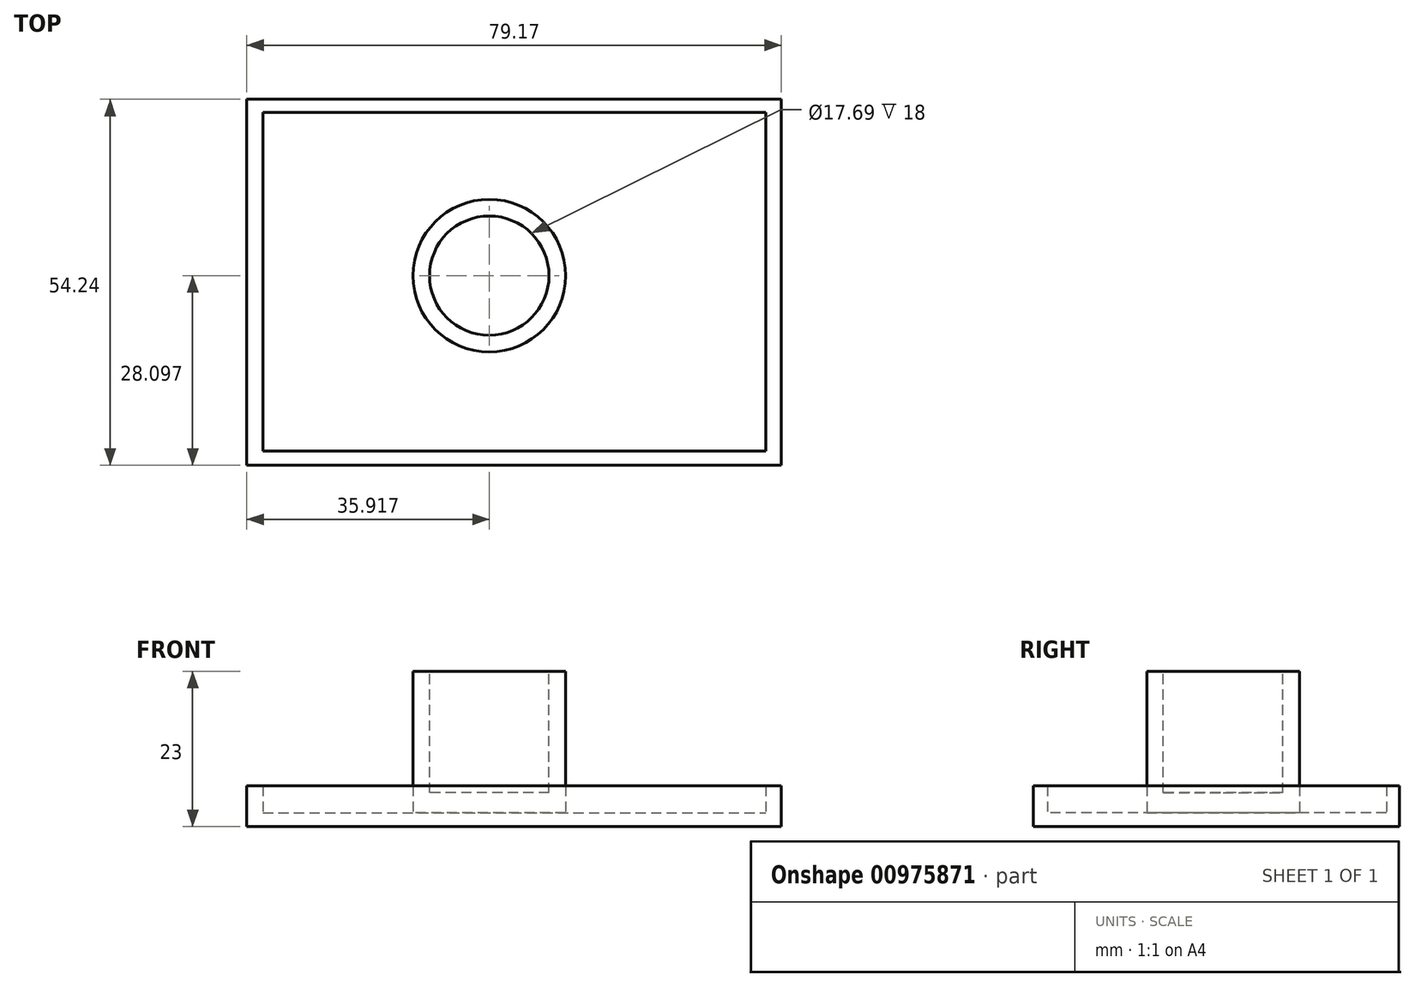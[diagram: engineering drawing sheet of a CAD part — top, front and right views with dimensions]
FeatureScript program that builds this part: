
annotation { "Feature Type Name" : "Feature", "Feature Type Description" : "" }
export const myFeature = defineFeature(function(context is Context, id is Id, definition is map)
    precondition{}
    {
        {
            var Q0;
            Q0=qCreatedBy(makeId("Top.planeOp"),FACE);
            var sketch = newSketch(context, id + "F0", { "sketchPlane" : qUnion([Q0])});
            skLineSegment(sketch, "E0.bottom", {"start": v(-67.35, 63.95) * mm, "end": v(11.82, 63.95) * mm});
            skLineSegment(sketch, "E0.top", {"start": v(-67.35, 9.7) * mm, "end": v(11.82, 9.7) * mm});
            skLineSegment(sketch, "E0.left", {"start": v(-67.35, 63.95) * mm, "end": v(-67.35, 9.7) * mm});
            skLineSegment(sketch, "E0.right", {"start": v(11.82, 63.95) * mm, "end": v(11.82, 9.7) * mm});
            skSolve(sketch);
        }
        {
            var Q0;
            Q0=makeQuery(id+"F0.imprint","IMPRINT",FACE,{"disambiguationData":[TD([[makeQuery(id+"F0.imprint","IMPRINT",EDGE,{"derivedFrom":sQuery(id+"F0.wireOp",EDGE,"E0.bottom")}),-1.0]])]});
            extrude(context, id + "F1", {"entities" : qUnion([Q0]), "depth" : 2 * mm, "offsetDistance" : 25 * mm});
        }
        {
            var Q0;
            Q0=makeQuery(id+"F1.opExtrude","CAP_FACE",FACE,{"disambiguationData":[OSD([sQuery(id+"F0.wireOp",EDGE,"E0.bottom"),sQuery(id+"F0.wireOp",EDGE,"E0.top"),sQuery(id+"F0.wireOp",EDGE,"E0.left"),sQuery(id+"F0.wireOp",EDGE,"E0.right")])],"isStart":false});
            var sketch = newSketch(context, id + "F2", { "sketchPlane" : qUnion([Q0])});
            skLineSegment(sketch, "E1.bottom", {"start": v(-67.35, 63.95) * mm, "end": v(11.82, 63.95) * mm});
            skLineSegment(sketch, "E1.top", {"start": v(-67.35, 62.02) * mm, "end": v(11.82, 62.02) * mm});
            skLineSegment(sketch, "E1.left", {"start": v(-67.35, 63.95) * mm, "end": v(-67.35, 62.02) * mm});
            skLineSegment(sketch, "E1.right", {"start": v(11.82, 63.95) * mm, "end": v(11.82, 62.02) * mm});
            skSolve(sketch);
        }
        {
            var Q0;
            Q0=makeQuery(id+"F2.imprint","IMPRINT",FACE,{"disambiguationData":[TD([[makeQuery(id+"F2.imprint","IMPRINT",EDGE,{"derivedFrom":sQuery(id+"F2.wireOp",EDGE,"E1.bottom")}),-1.0]])]});
            extrude(context, id + "F3", {"entities" : qUnion([Q0]), "operationType" : NewBodyOperationType.ADD, "depth" : 4 * mm, "offsetDistance" : 25 * mm});
        }
        {
            var Q0;
            Q0=makeQuery(id+"F3.boolean.opBoolean","MERGE",FACE,{"derivedFrom":[makeQuery(id+"F1.opExtrude","SWEPT_FACE",FACE,{"disambiguationData":[OSD([sQuery(id+"F0.wireOp",EDGE,"E0.right")])]}),makeQuery(id+"F3.opExtrude","SWEPT_FACE",FACE,{"disambiguationData":[OSD([sQuery(id+"F2.wireOp",EDGE,"E1.right")])]})]});
            var sketch = newSketch(context, id + "F4", { "sketchPlane" : qUnion([Q0])});
            skLineSegment(sketch, "E2.bottom", {"start": v(62.02, 6) * mm, "end": v(9.7, 6) * mm});
            skLineSegment(sketch, "E2.top", {"start": v(62.02, 2) * mm, "end": v(9.7, 2) * mm});
            skLineSegment(sketch, "E2.left", {"start": v(62.02, 6) * mm, "end": v(62.02, 2) * mm});
            skLineSegment(sketch, "E2.right", {"start": v(9.7, 6) * mm, "end": v(9.7, 2) * mm});
            skSolve(sketch);
        }
        {
            var Q0;
            Q0=makeQuery(id+"F4.imprint","IMPRINT",FACE,{"disambiguationData":[TD([[makeQuery(id+"F4.imprint","IMPRINT",EDGE,{"derivedFrom":sQuery(id+"F4.wireOp",EDGE,"E2.bottom")}),1.0]])]});
            extrude(context, id + "F5", {"entities" : qUnion([Q0]), "operationType" : NewBodyOperationType.ADD, "oppositeDirection" : true, "depth" : 2.3 * mm, "offsetDistance" : 25 * mm});
        }
        {
            var Q0;
            Q0=makeQuery(id+"F5.boolean.opBoolean","MERGE",FACE,{"derivedFrom":[makeQuery(id+"F1.opExtrude","SWEPT_FACE",FACE,{"disambiguationData":[OSD([sQuery(id+"F0.wireOp",EDGE,"E0.top")])]}),makeQuery(id+"F5.opExtrude","SWEPT_FACE",FACE,{"disambiguationData":[OSD([sQuery(id+"F4.wireOp",EDGE,"E2.right")])]})]});
            var sketch = newSketch(context, id + "F6", { "sketchPlane" : qUnion([Q0])});
            skLineSegment(sketch, "E3.bottom", {"start": v(-67.35, 2) * mm, "end": v(9.52, 2) * mm});
            skLineSegment(sketch, "E3.top", {"start": v(-67.35, 6) * mm, "end": v(9.52, 6) * mm});
            skLineSegment(sketch, "E3.left", {"start": v(-67.35, 2) * mm, "end": v(-67.35, 6) * mm});
            skLineSegment(sketch, "E3.right", {"start": v(9.52, 2) * mm, "end": v(9.52, 6) * mm});
            skSolve(sketch);
        }
        {
            var Q0;
            Q0 = qSketchRegion(id + "F6", true);
            extrude(context, id + "F7", {"entities" : qUnion([Q0]), "operationType" : NewBodyOperationType.ADD, "oppositeDirection" : true, "depth" : 2.1 * mm, "offsetDistance" : 25 * mm});
        }
        {
            var Q0;
            Q0=makeQuery(id+"F7.boolean.opBoolean","MERGE",FACE,{"derivedFrom":[makeQuery(id+"F3.boolean.opBoolean","MERGE",FACE,{"derivedFrom":[makeQuery(id+"F1.opExtrude","SWEPT_FACE",FACE,{"disambiguationData":[OSD([sQuery(id+"F0.wireOp",EDGE,"E0.left")])]}),makeQuery(id+"F3.opExtrude","SWEPT_FACE",FACE,{"disambiguationData":[OSD([sQuery(id+"F2.wireOp",EDGE,"E1.left")])]})]}),makeQuery(id+"F7.opExtrude","SWEPT_FACE",FACE,{"disambiguationData":[OSD([sQuery(id+"F6.wireOp",EDGE,"E3.left")])]})]});
            var sketch = newSketch(context, id + "F8", { "sketchPlane" : qUnion([Q0])});
            skLineSegment(sketch, "E4.bottom", {"start": v(-62.02, 2) * mm, "end": v(-11.8, 2) * mm});
            skLineSegment(sketch, "E4.top", {"start": v(-62.02, 6) * mm, "end": v(-11.8, 6) * mm});
            skLineSegment(sketch, "E4.left", {"start": v(-62.02, 2) * mm, "end": v(-62.02, 6) * mm});
            skLineSegment(sketch, "E4.right", {"start": v(-11.8, 2) * mm, "end": v(-11.8, 6) * mm});
            skSolve(sketch);
        }
        {
            var Q0;
            Q0 = qSketchRegion(id + "F8", true);
            extrude(context, id + "F9", {"entities" : qUnion([Q0]), "operationType" : NewBodyOperationType.ADD, "oppositeDirection" : true, "depth" : 2.4 * mm, "offsetDistance" : 25 * mm});
        }
        {
            var Q0;
            Q0=makeQuery(id+"F1.opExtrude","CAP_FACE",FACE,{"disambiguationData":[OSD([sQuery(id+"F0.wireOp",EDGE,"E0.bottom"),sQuery(id+"F0.wireOp",EDGE,"E0.top"),sQuery(id+"F0.wireOp",EDGE,"E0.left"),sQuery(id+"F0.wireOp",EDGE,"E0.right")])],"isStart":false});
            var sketch = newSketch(context, id + "F10", { "sketchPlane" : qUnion([Q0])});
            skCircle(sketch, "E5", {"center": v(-31.43, 37.8) * mm, "radius": 11.3 * mm});
            skSolve(sketch);
        }
        {
            var Q0;
            Q0 = qSketchRegion(id + "F10", true);
            extrude(context, id + "F11", {"entities" : qUnion([Q0]), "operationType" : NewBodyOperationType.ADD, "depth" : 21 * mm, "offsetDistance" : 25 * mm});
        }
        {
            var Q0;
            Q0=makeQuery(id+"F11.opExtrude","CAP_FACE",FACE,{"disambiguationData":[OSD([sQuery(id+"F10.wireOp",EDGE,"E5")])],"isStart":false});
            var sketch = newSketch(context, id + "F12", { "sketchPlane" : qUnion([Q0])});
            skCircle(sketch, "E6", {"center": v(-31.43, 37.8) * mm, "radius": 9.8 * mm});
            skSolve(sketch);
        }
        {
            var Q0;
            Q0 = qSketchRegion(id + "F12", true);
            extrude(context, id + "F13", {"entities" : qUnion([Q0]), "operationType" : NewBodyOperationType.ADD, "oppositeDirection" : true, "depth" : 11 * mm, "offsetDistance" : 25 * mm});
        }
        {
            var Q0;
            Q0=makeQuery(id+"F11.opExtrude","CAP_FACE",FACE,{"disambiguationData":[OSD([sQuery(id+"F10.wireOp",EDGE,"E5")])],"isStart":false});
            var sketch = newSketch(context, id + "F14", { "sketchPlane" : qUnion([Q0])});
            skCircle(sketch, "E7", {"center": v(-31.43, 37.8) * mm, "radius": 8.84 * mm});
            skSolve(sketch);
        }
        {
            var Q0;
            Q0=makeQuery(id+"F14.imprint","IMPRINT",FACE,{"disambiguationData":[TD([[makeQuery(id+"F14.imprint","IMPRINT",EDGE,{"derivedFrom":sQuery(id+"F14.wireOp",EDGE,"E7")}),1.0]])]});
            extrude(context, id + "F15", {"entities" : qUnion([Q0]), "operationType" : NewBodyOperationType.REMOVE, "oppositeDirection" : true, "depth" : 18 * mm, "offsetDistance" : 25 * mm});
        }
    });
